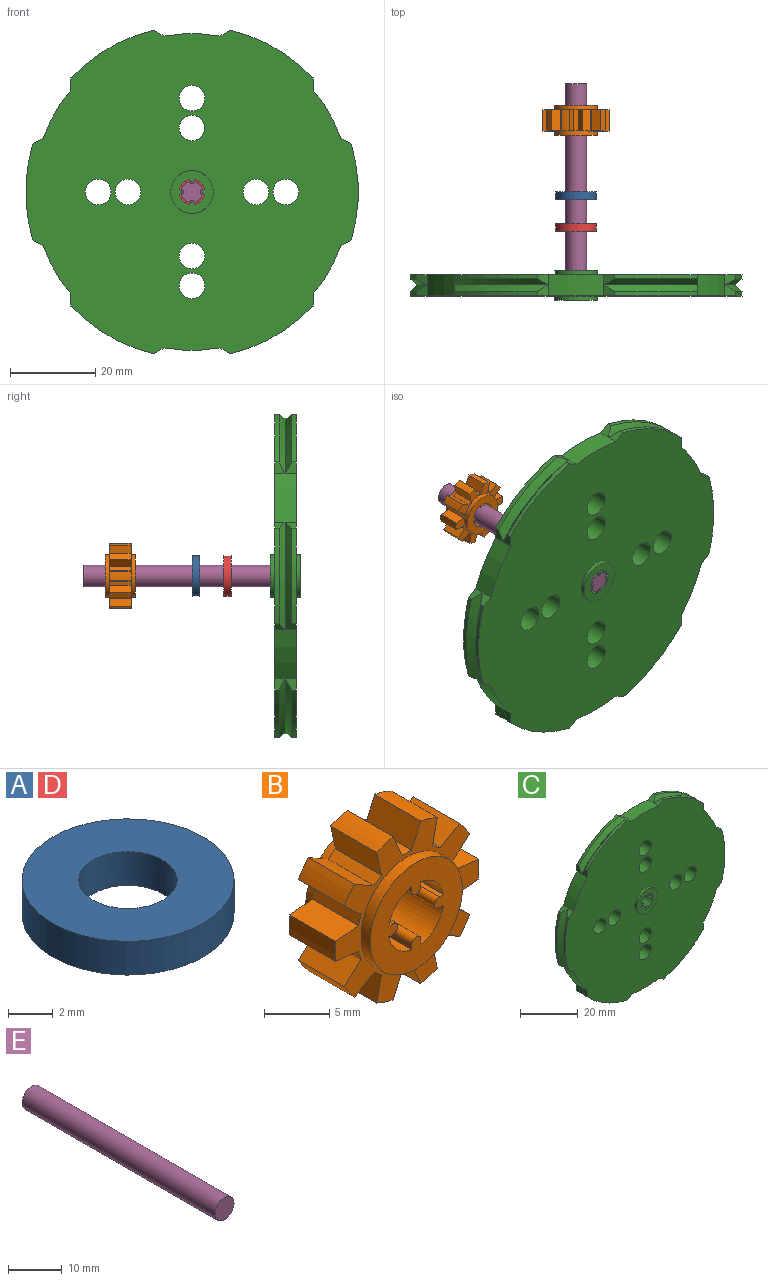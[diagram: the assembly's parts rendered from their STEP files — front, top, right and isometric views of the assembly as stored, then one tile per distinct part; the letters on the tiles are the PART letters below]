
ASSEMBLY  parts=5 mates=4
PART A: 4 faces, bbox 9.5x9.5x1.9 mm
  f0: cylinder r=2.21mm len=4.42mm, axis (0,0,1), area 25.7mm2, adj f1,f3
  f1: plane 9.53x9.53mm, normal (0,0,-1), area 55.9mm2, adj f0,f2
  f2: cylinder r=4.76mm len=9.53mm, axis (0,0,-1), area 55.5mm2, adj f1,f3
  f3: plane 9.53x9.53mm, normal (0,0,1), area 55.9mm2, adj f0,f2
PART B: 62 faces, bbox 15.6x7x15.3 mm
  f0: plane 15.6x15.31mm, normal (0,1,0), area 64.7mm2, adj f1,f7,f8,f9,f10,f11,f12,f13
  f1: cylinder r=5mm len=10mm, axis (0,1,0), area 31.4mm2, adj f0,f2
  f2: plane 10x10mm, normal (0,1,0), area 53.8mm2, adj f1,f3,f47,f48,f49,f50,f51,f52
  f3: cylinder r=0.5mm len=7mm, axis (0,-1,0), area 11mm2, adj f2,f4,f47,f58
  f4: plane 10x10mm, normal (0,-1,0), area 53.8mm2, adj f3,f5,f47,f48,f49,f50,f51,f52
  f5: cylinder r=5mm len=10mm, axis (0,-1,0), area 31.4mm2, adj f4,f6
  f6: plane 15.6x15.31mm, normal (0,-1,0), area 64.7mm2, adj f5,f7,f8,f9,f10,f11,f12,f13
  f7: plane 5x0.81mm, normal (-0.59,0,0.81), area 5mm2, adj f0,f6,f8,f46
  f8: plane 5x2.41mm, normal (-0.98,0,-0.21), area 12.3mm2, adj f0,f6,f7,f18
  f9: cylinder r=7.8mm len=5mm, axis (0,-1,0), area 9.4mm2, adj f0,f6,f19,f22
  f10: cylinder r=7.8mm len=5mm, axis (0,-1,0), area 9.4mm2, adj f0,f6,f21,f25
  f11: cylinder r=7.8mm len=5mm, axis (0,-1,0), area 9.4mm2, adj f0,f6,f27,f28
  f12: cylinder r=7.8mm len=5mm, axis (0,-1,0), area 9.4mm2, adj f0,f6,f30,f31
  f13: cylinder r=7.8mm len=5mm, axis (0,-1,0), area 9.4mm2, adj f0,f6,f33,f34
  f14: cylinder r=7.8mm len=5mm, axis (0,-1,0), area 9.4mm2, adj f0,f6,f36,f37
  f15: cylinder r=7.8mm len=5mm, axis (0,-1,0), area 9.4mm2, adj f0,f6,f39,f40
  f16: cylinder r=7.8mm len=5mm, axis (0,-1,0), area 9.4mm2, adj f0,f6,f42,f43
  f17: cylinder r=7.8mm len=5mm, axis (0,-1,0), area 9.4mm2, adj f0,f6,f45,f46
  f18: cylinder r=7.8mm len=5mm, axis (0,-1,0), area 9.4mm2, adj f0,f6,f8,f24
  f19: plane 5x2.41mm, normal (0.98,0,-0.21), area 12.3mm2, adj f0,f6,f9,f20
  f20: plane 5x0.81mm, normal (0.59,0,0.81), area 5mm2, adj f0,f6,f19,f21
  f21: plane 5x2.13mm, normal (-0.5,0,0.87), area 12.3mm2, adj f0,f6,f10,f20
  f22: plane 5x2.25mm, normal (-0.91,0,0.41), area 12.3mm2, adj f0,f6,f9,f23
  f23: plane 5x1mm, normal (0,0,1), area 5mm2, adj f0,f6,f22,f24
  f24: plane 5x2.25mm, normal (0.91,0,0.41), area 12.3mm2, adj f0,f6,f18,f23
  f25: plane 5x1.83mm, normal (0.67,0,-0.74), area 12.3mm2, adj f0,f6,f10,f26
  f26: plane 5x0.95mm, normal (0.95,0,0.31), area 5mm2, adj f0,f6,f25,f27
  f27: plane 5x2.45mm, normal (0.1,0,0.99), area 12.3mm2, adj f0,f6,f11,f26
  f28: plane 5x2.45mm, normal (0.1,0,-0.99), area 12.3mm2, adj f0,f6,f11,f29
  f29: plane 5x0.95mm, normal (0.95,0,-0.31), area 5mm2, adj f0,f6,f28,f30
  f30: plane 5x1.83mm, normal (0.67,0,0.74), area 12.3mm2, adj f0,f6,f12,f29
  f31: plane 5x2.13mm, normal (-0.5,0,-0.87), area 12.3mm2, adj f0,f6,f12,f32
  f32: plane 5x0.81mm, normal (0.59,0,-0.81), area 5mm2, adj f0,f6,f31,f33
  f33: plane 5x2.41mm, normal (0.98,0,0.21), area 12.3mm2, adj f0,f6,f13,f32
  f34: plane 5x2.25mm, normal (-0.91,0,-0.41), area 12.3mm2, adj f0,f6,f13,f35
  f35: plane 5x1mm, normal (0,0,-1), area 5mm2, adj f0,f6,f34,f36
  f36: plane 5x2.25mm, normal (0.91,0,-0.41), area 12.3mm2, adj f0,f6,f14,f35
  f37: plane 5x2.41mm, normal (-0.98,0,0.21), area 12.3mm2, adj f0,f6,f14,f38
  f38: plane 5x0.81mm, normal (-0.59,0,-0.81), area 5mm2, adj f0,f6,f37,f39
  f39: plane 5x2.13mm, normal (0.5,0,-0.87), area 12.3mm2, adj f0,f6,f15,f38
  f40: plane 5x1.83mm, normal (-0.67,0,0.74), area 12.3mm2, adj f0,f6,f15,f41
  f41: plane 5x0.95mm, normal (-0.95,0,-0.31), area 5mm2, adj f0,f6,f40,f42
  f42: plane 5x2.45mm, normal (-0.1,0,-0.99), area 12.3mm2, adj f0,f6,f16,f41
  f43: plane 5x2.45mm, normal (-0.1,0,0.99), area 12.3mm2, adj f0,f6,f16,f44
  f44: plane 5x0.95mm, normal (-0.95,0,0.31), area 5mm2, adj f0,f6,f43,f45
  f45: plane 5x1.83mm, normal (-0.67,0,-0.74), area 12.3mm2, adj f0,f6,f17,f44
  f46: plane 5x2.13mm, normal (0.5,0,0.87), area 12.3mm2, adj f0,f6,f7,f17
  f47: plane 7x0.46mm, normal (-1,0,0), area 3.2mm2, adj f2,f3,f4,f48
  f48: cylinder r=3mm len=7mm, axis (0,1,0), area 26mm2, adj f2,f4,f47,f52
  f49: cylinder r=3mm len=7mm, axis (0,1,0), area 26mm2, adj f2,f4,f55,f58
  f50: cylinder r=3mm len=7mm, axis (0,1,0), area 26mm2, adj f2,f4,f57,f59
  f51: cylinder r=3mm len=7mm, axis (0,1,0), area 26mm2, adj f2,f4,f54,f61
  f52: plane 7x0.46mm, normal (0,0,1), area 3.2mm2, adj f2,f4,f48,f53
  f53: cylinder r=0.5mm len=7mm, axis (0,-1,0), area 11mm2, adj f2,f4,f52,f54
  f54: plane 7x0.46mm, normal (0,0,-1), area 3.2mm2, adj f2,f4,f51,f53
  f55: plane 7x0.46mm, normal (0,0,1), area 3.2mm2, adj f2,f4,f49,f56
  f56: cylinder r=0.5mm len=7mm, axis (0,-1,0), area 11mm2, adj f2,f4,f55,f57
  f57: plane 7x0.46mm, normal (0,0,-1), area 3.2mm2, adj f2,f4,f50,f56
  f58: plane 7x0.46mm, normal (1,0,0), area 3.2mm2, adj f2,f3,f4,f49
  f59: plane 7x0.46mm, normal (1,0,0), area 3.2mm2, adj f2,f4,f50,f60
  f60: cylinder r=0.5mm len=7mm, axis (0,-1,0), area 11mm2, adj f2,f4,f59,f61
  f61: plane 7x0.46mm, normal (-1,0,0), area 3.2mm2, adj f2,f4,f51,f60
PART C: 84 faces, bbox 78x7x76.7 mm
  f0: plane 77.96x75.87mm, normal (0,1,0), area 4294.7mm2, adj f2,f6,f10,f14,f18,f22,f24,f25
  f1: cylinder r=38.98mm len=19.42mm, axis (0,-1,0), area 23.1mm2, adj f23,f52,f55,f82
  f2: cylinder r=38.98mm len=19.42mm, axis (0,-1,0), area 23.1mm2, adj f0,f53,f56,f83
  f3: cone r=37.13mm half-angle=49.6deg, axis (0,-1,0), area 59mm2, adj f4,f5,f77,f80
  f4: cone r=38.98mm half-angle=53.2deg, axis (0,1,0), area 56.1mm2, adj f3,f6,f78,f81
  f5: cylinder r=38.98mm len=22.42mm, axis (0,-1,0), area 23.1mm2, adj f3,f23,f77,f80
  f6: cylinder r=38.98mm len=22.42mm, axis (0,-1,0), area 23.1mm2, adj f0,f4,f78,f81
  f7: cone r=37.13mm half-angle=49.6deg, axis (0,-1,0), area 59mm2, adj f8,f9,f72,f75
  f8: cone r=38.98mm half-angle=53.2deg, axis (0,1,0), area 56.1mm2, adj f7,f10,f73,f76
  f9: cylinder r=38.98mm len=19.42mm, axis (0,-1,0), area 23.1mm2, adj f7,f23,f72,f75
  f10: cylinder r=38.98mm len=19.42mm, axis (0,-1,0), area 23.1mm2, adj f0,f8,f73,f76
  f11: cone r=37.13mm half-angle=49.6deg, axis (0,-1,0), area 59mm2, adj f12,f13,f67,f70
  f12: cone r=38.98mm half-angle=53.2deg, axis (0,1,0), area 56.1mm2, adj f11,f14,f68,f71
  f13: cylinder r=38.98mm len=19.42mm, axis (0,-1,0), area 23.1mm2, adj f11,f23,f67,f70
  f14: cylinder r=38.98mm len=19.42mm, axis (0,-1,0), area 23.1mm2, adj f0,f12,f68,f71
  f15: cone r=37.13mm half-angle=49.6deg, axis (0,-1,0), area 59mm2, adj f16,f17,f62,f65
  f16: cone r=38.98mm half-angle=53.2deg, axis (0,1,0), area 56.1mm2, adj f15,f18,f63,f66
  f17: cylinder r=38.98mm len=22.42mm, axis (0,-1,0), area 23.1mm2, adj f15,f23,f62,f65
  f18: cylinder r=38.98mm len=22.42mm, axis (0,-1,0), area 23.1mm2, adj f0,f16,f63,f66
  f19: cone r=37.13mm half-angle=49.6deg, axis (0,-1,0), area 59mm2, adj f20,f21,f57,f60
  f20: cone r=38.98mm half-angle=53.2deg, axis (0,1,0), area 56.1mm2, adj f19,f22,f58,f61
  f21: cylinder r=38.98mm len=19.42mm, axis (0,-1,0), area 23.1mm2, adj f19,f23,f57,f60
  f22: cylinder r=38.98mm len=19.42mm, axis (0,-1,0), area 23.1mm2, adj f0,f20,f58,f61
  f23: plane 77.96x75.87mm, normal (0,-1,0), area 4294.7mm2, adj f1,f5,f9,f13,f17,f21,f24,f25
  f24: cylinder r=3mm len=6mm, axis (0,1,0), area 94.2mm2, adj f0,f23
  f25: cylinder r=3mm len=6mm, axis (0,1,0), area 94.2mm2, adj f0,f23
  f26: cylinder r=3mm len=6mm, axis (0,1,0), area 94.2mm2, adj f0,f23
  f27: cylinder r=3mm len=6mm, axis (0,1,0), area 94.2mm2, adj f0,f23
  f28: cylinder r=3mm len=6mm, axis (0,-1,0), area 94.2mm2, adj f0,f23
  f29: cylinder r=3mm len=7mm, axis (0,-1,0), area 26mm2, adj f36,f38,f41,f44
  f30: cylinder r=3mm len=6mm, axis (0,-1,0), area 94.2mm2, adj f0,f23
  f31: cylinder r=5mm len=10mm, axis (0,1,0), area 31.4mm2, adj f23,f38
  f32: plane 7x0.46mm, normal (0,0,1), area 3.2mm2, adj f37,f38,f41,f47
  f33: plane 7x0.46mm, normal (-1,0,0), area 3.2mm2, adj f38,f39,f41,f46
  f34: plane 7x0.46mm, normal (1,0,0), area 3.2mm2, adj f38,f39,f41,f47
  f35: plane 7x0.46mm, normal (0,0,1), area 3.2mm2, adj f38,f41,f45,f46
  f36: plane 7x0.46mm, normal (-1,0,0), area 3.2mm2, adj f29,f38,f41,f50
  f37: cylinder r=0.5mm len=7mm, axis (0,1,0), area 11mm2, adj f32,f38,f40,f41
  f38: plane 10x10mm, normal (0,-1,0), area 53.8mm2, adj f29,f31,f32,f33,f34,f35,f36,f37
  f39: cylinder r=0.5mm len=7mm, axis (0,1,0), area 11mm2, adj f33,f34,f38,f41
  f40: plane 7x0.46mm, normal (0,0,-1), area 3.2mm2, adj f37,f38,f41,f48
  f41: plane 10x10mm, normal (0,1,0), area 53.8mm2, adj f29,f32,f33,f34,f35,f36,f37,f39
  f42: cylinder r=5mm len=10mm, axis (0,-1,0), area 31.4mm2, adj f0,f41
  f43: cylinder r=3mm len=6mm, axis (0,-1,0), area 94.2mm2, adj f0,f23
  f44: plane 7x0.46mm, normal (0,0,-1), area 3.2mm2, adj f29,f38,f41,f45
  f45: cylinder r=0.5mm len=7mm, axis (0,1,0), area 11mm2, adj f35,f38,f41,f44
  f46: cylinder r=3mm len=7mm, axis (0,-1,0), area 26mm2, adj f33,f35,f38,f41
  f47: cylinder r=3mm len=7mm, axis (0,-1,0), area 26mm2, adj f32,f34,f38,f41
  f48: cylinder r=3mm len=7mm, axis (0,-1,0), area 26mm2, adj f38,f40,f41,f49
  f49: plane 7x0.46mm, normal (1,0,0), area 3.2mm2, adj f38,f41,f48,f50
  f50: cylinder r=0.5mm len=7mm, axis (0,1,0), area 11mm2, adj f36,f38,f41,f49
  f51: cylinder r=3mm len=6mm, axis (0,-1,0), area 94.2mm2, adj f0,f23
  f52: cone r=37.13mm half-angle=49.6deg, axis (0,-1,0), area 59mm2, adj f1,f53,f55,f82
  f53: cone r=38.98mm half-angle=53.2deg, axis (0,1,0), area 56.1mm2, adj f2,f52,f56,f83
  f54: cylinder r=37.13mm len=13.09mm, axis (0,-1,0), area 65.8mm2, adj f0,f23,f55,f56,f57,f58
  f55: plane 2.6x2.41mm, normal (-0.5,0,0.87), area 5.1mm2, adj f1,f23,f52,f54
  f56: plane 2.41x2.4mm, normal (-0.5,0,0.87), area 4.8mm2, adj f0,f2,f53,f54
  f57: plane 2.6x2.41mm, normal (0.5,0,0.87), area 5.1mm2, adj f19,f21,f23,f54
  f58: plane 2.41x2.4mm, normal (0.5,0,0.87), area 4.8mm2, adj f0,f20,f22,f54
  f59: cylinder r=37.13mm len=11.34mm, axis (0,-1,0), area 65.8mm2, adj f0,f23,f60,f61,f62,f63
  f60: plane 2.79x2.6mm, normal (-1,0,0), area 5.1mm2, adj f19,f21,f23,f59
  f61: plane 2.79x2.41mm, normal (-1,0,0), area 4.8mm2, adj f0,f20,f22,f59
  f62: plane 2.6x2.41mm, normal (-0.5,0,0.87), area 5.1mm2, adj f15,f17,f23,f59
  f63: plane 2.41x2.4mm, normal (-0.5,0,0.87), area 4.8mm2, adj f0,f16,f18,f59
  f64: cylinder r=37.13mm len=11.34mm, axis (0,-1,0), area 65.8mm2, adj f0,f23,f65,f66,f67,f68
  f65: plane 2.6x2.41mm, normal (-0.5,0,-0.87), area 5.1mm2, adj f15,f17,f23,f64
  f66: plane 2.41x2.4mm, normal (-0.5,0,-0.87), area 4.8mm2, adj f0,f16,f18,f64
  f67: plane 2.79x2.6mm, normal (-1,0,0), area 5.1mm2, adj f11,f13,f23,f64
  f68: plane 2.79x2.41mm, normal (-1,0,0), area 4.8mm2, adj f0,f12,f14,f64
  f69: cylinder r=37.13mm len=13.09mm, axis (0,-1,0), area 65.8mm2, adj f0,f23,f70,f71,f72,f73
  f70: plane 2.6x2.41mm, normal (0.5,0,-0.87), area 5.1mm2, adj f11,f13,f23,f69
  f71: plane 2.41x2.4mm, normal (0.5,0,-0.87), area 4.8mm2, adj f0,f12,f14,f69
  f72: plane 2.6x2.41mm, normal (-0.5,0,-0.87), area 5.1mm2, adj f7,f9,f23,f69
  f73: plane 2.41x2.4mm, normal (-0.5,0,-0.87), area 4.8mm2, adj f0,f8,f10,f69
  f74: cylinder r=37.13mm len=11.34mm, axis (0,-1,0), area 65.8mm2, adj f0,f23,f75,f76,f77,f78
  f75: plane 2.79x2.6mm, normal (1,0,0), area 5.1mm2, adj f7,f9,f23,f74
  f76: plane 2.79x2.41mm, normal (1,0,0), area 4.8mm2, adj f0,f8,f10,f74
  f77: plane 2.6x2.41mm, normal (0.5,0,-0.87), area 5.1mm2, adj f3,f5,f23,f74
  f78: plane 2.41x2.4mm, normal (0.5,0,-0.87), area 4.8mm2, adj f0,f4,f6,f74
  f79: cylinder r=37.13mm len=11.34mm, axis (0,-1,0), area 65.8mm2, adj f0,f23,f80,f81,f82,f83
  f80: plane 2.6x2.41mm, normal (0.5,0,0.87), area 5.1mm2, adj f3,f5,f23,f79
  f81: plane 2.41x2.4mm, normal (0.5,0,0.87), area 4.8mm2, adj f0,f4,f6,f79
  f82: plane 2.79x2.6mm, normal (1,0,0), area 5.1mm2, adj f1,f23,f52,f79
  f83: plane 2.79x2.41mm, normal (1,0,0), area 4.8mm2, adj f0,f2,f53,f79
PART D: same geometry as A
PART E: 3 faces, bbox 5x50.8x5 mm
  f0: cylinder r=2.5mm len=50.8mm, axis (0,1,0), area 798mm2, adj f1,f2
  f1: plane 5x5mm, normal (0,-1,0), area 19.6mm2, adj f0
  f2: plane 5x5mm, normal (0,1,0), area 19.6mm2, adj f0
PLACE A rot(axis=(1,0,0),90deg) t=(-31.65,-1.02,-13.74)mm
PLACE B t=(-31.65,18.27,-13.74)mm
PLACE C t=(-31.65,-20.42,-13.74)mm
PLACE D rot(axis=(-1,0,0),90deg) t=(-31.65,-10.27,-13.74)mm
PLACE E t=(-64.61,24.38,-75.08)mm
MATE cylindrical A.f0 <-> E.f0  axis (0,1,0) through (-31.65,-1.02,-13.74)mm
MATE cylindrical B.f1 <-> E.f0  axis (0,1,0) through (-31.65,19.27,-13.74)mm
MATE cylindrical D.f0 <-> E.f0  axis (0,1,0) through (-31.65,-8.41,-13.74)mm
MATE cylindrical E.f0 <-> C.f1  axis (0,1,0) through (-31.65,-26.42,-13.74)mm
